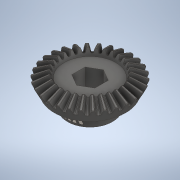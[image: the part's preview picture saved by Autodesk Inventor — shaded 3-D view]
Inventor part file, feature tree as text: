
AUTODESK INVENTOR PART (.ipt)
format: ipt  version: 2020 (Build 240168000, 168)  size: 1,947,648 bytes
history: native  units: in
note: dims shown in document units (in); Inventor stores cm internally (conversion verified against a paired STEP export)
features: extrude x1, sketch x1, imported_body x1
ambient origin geometry x8: Origin, YZ Plane, XZ Plane, XY Plane, X Axis, Y Axis, Z Axis, Center Point
bodies: Solid1 (feature_tree)
feature tree (3):
  extrude  "Extrusion2"  TaperAngle=0.0deg  [1 undecoded]
  sketch  "Sketch2"  dims[d3=0.5in d4=0.0in d5=0.0in]
  imported_body  "Base1"
note: 1 required parameter value undecoded (feature->parameter linkage not recoverable at this tier; creation-order binding heuristic only, values carry confidence <= 0.55)
